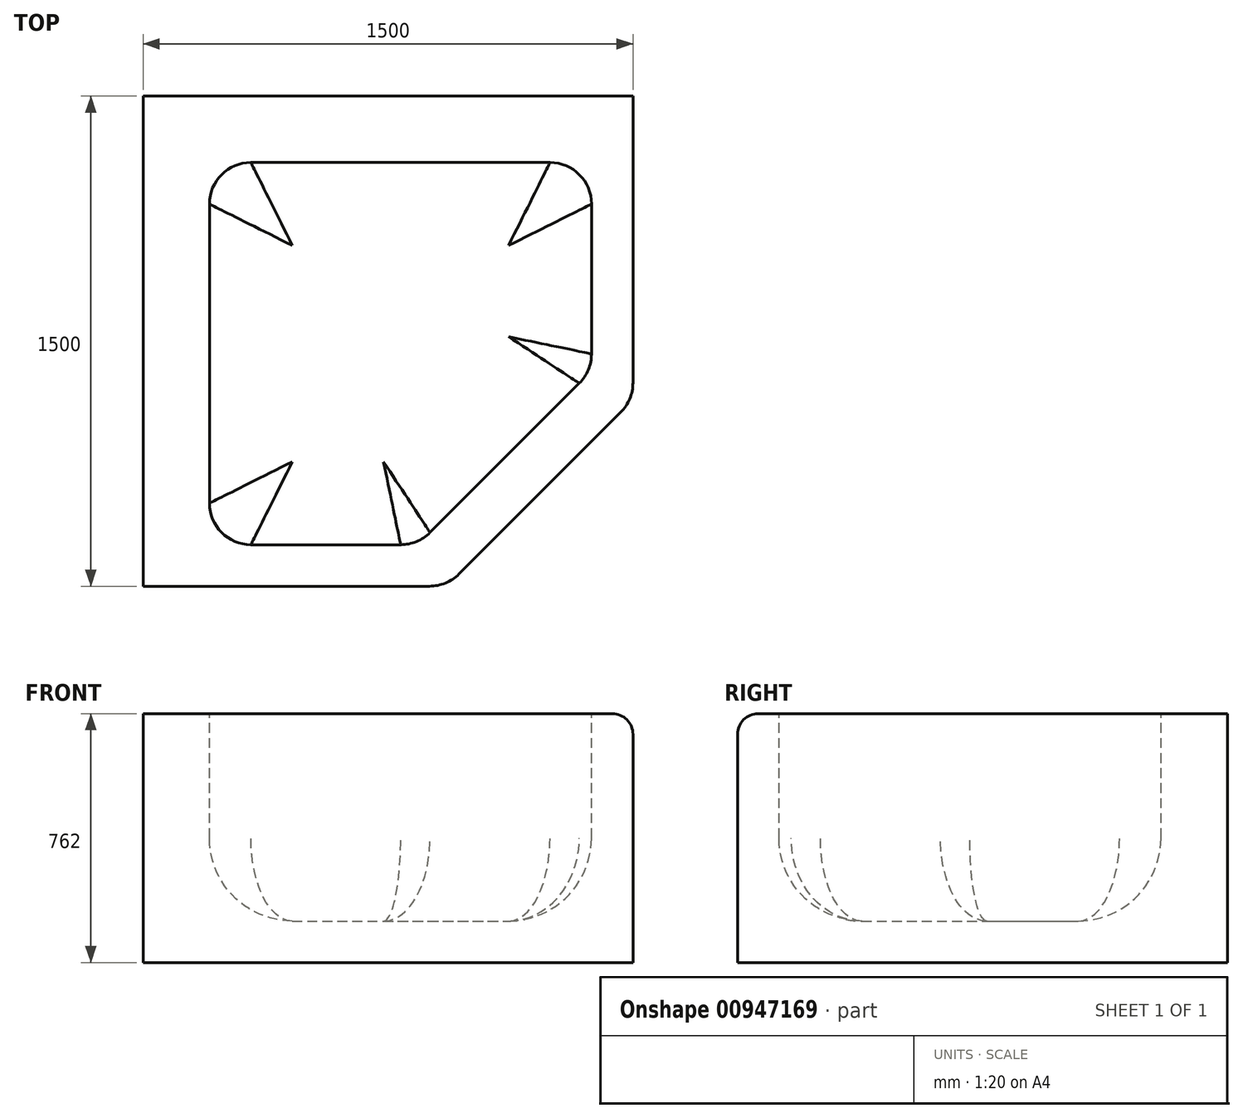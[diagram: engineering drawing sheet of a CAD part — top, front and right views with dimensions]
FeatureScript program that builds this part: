
annotation { "Feature Type Name" : "Feature", "Feature Type Description" : "" }
export const myFeature = defineFeature(function(context is Context, id is Id, definition is map)
    precondition{}
    {
        {
            var Q0;
            Q0=qCreatedBy(makeId("Top.planeOp"),FACE);
            var sketch = newSketch(context, id + "F0", { "sketchPlane" : qUnion([Q0])});
            skLineSegment(sketch, "E0", {"start": v(0, 0) * mm, "end": v(-1500, 0) * mm});
            skLineSegment(sketch, "E1", {"start": v(-1500, 0) * mm, "end": v(-1500, -1500) * mm});
            skLineSegment(sketch, "E2", {"start": v(-1500, -1500) * mm, "end": v(-570, -1500) * mm});
            skLineSegment(sketch, "E3", {"start": v(0, 0) * mm, "end": v(0, -930) * mm});
            skLineSegment(sketch, "E4", {"start": v(-570, -1500) * mm, "end": v(0, -930) * mm});
            skSolve(sketch);
        }
        {
            var Q0;
            Q0 = qSketchRegion(id + "F0", true);
            extrude(context, id + "F1", {"entities" : qUnion([Q0]), "depth" : 762 * mm, "offsetDistance" : 25.4 * mm});
        }
        {
            var Q0;
            Q0=makeQuery(id+"F1.opExtrude","CAP_FACE",FACE,{"disambiguationData":[OSD([sQuery(id+"F0.wireOp",EDGE,"E0"),sQuery(id+"F0.wireOp",EDGE,"E1"),sQuery(id+"F0.wireOp",EDGE,"E2"),sQuery(id+"F0.wireOp",EDGE,"E3"),sQuery(id+"F0.wireOp",EDGE,"E4")])],"isStart":false});
            var sketch = newSketch(context, id + "F2", { "sketchPlane" : qUnion([Q0])});
            skLineSegment(sketch, "E5", {"start": v(-1296.8, -1373) * mm, "end": v(-658.53, -1373) * mm});
            skLineSegment(sketch, "E6", {"start": v(-658.53, -1373) * mm, "end": v(-127, -841.47) * mm});
            skLineSegment(sketch, "E7", {"start": v(-127, -841.47) * mm, "end": v(-127, -203.2) * mm});
            skLineSegment(sketch, "E8", {"start": v(-1296.8, -1373) * mm, "end": v(-1296.8, -203.2) * mm});
            skLineSegment(sketch, "E9", {"start": v(-1296.8, -203.2) * mm, "end": v(-127, -203.2) * mm});
            skSolve(sketch);
        }
        {
            var Q0;
            Q0 = qSketchRegion(id + "F2", true);
            extrude(context, id + "F3", {"entities" : qUnion([Q0]), "operationType" : NewBodyOperationType.REMOVE, "oppositeDirection" : true, "depth" : 635 * mm, "offsetDistance" : 25.4 * mm});
        }
        {
            var Q0;
            Q0=makeQuery(id+"F3.boolean.opBoolean","COPY",EDGE,{"derivedFrom":makeQuery(id+"F3.opExtrude","CAP_EDGE",EDGE,{"disambiguationData":[OSD([sQuery(id+"F2.wireOp",EDGE,"E9")])],"isStart":false})});
            var Q1;
            Q1=makeQuery(id+"F3.boolean.opBoolean","COPY",EDGE,{"derivedFrom":makeQuery(id+"F3.opExtrude","CAP_EDGE",EDGE,{"disambiguationData":[OSD([sQuery(id+"F2.wireOp",EDGE,"E8")])],"isStart":false})});
            var Q2;
            Q2=makeQuery(id+"F3.boolean.opBoolean","COPY",EDGE,{"derivedFrom":makeQuery(id+"F3.opExtrude","CAP_EDGE",EDGE,{"disambiguationData":[OSD([sQuery(id+"F2.wireOp",EDGE,"E5")])],"isStart":false})});
            var Q3;
            Q3=makeQuery(id+"F3.boolean.opBoolean","COPY",EDGE,{"derivedFrom":makeQuery(id+"F3.opExtrude","CAP_EDGE",EDGE,{"disambiguationData":[OSD([sQuery(id+"F2.wireOp",EDGE,"E6")])],"isStart":false})});
            var Q4;
            Q4=makeQuery(id+"F3.boolean.opBoolean","COPY",EDGE,{"derivedFrom":makeQuery(id+"F3.opExtrude","CAP_EDGE",EDGE,{"disambiguationData":[OSD([sQuery(id+"F2.wireOp",EDGE,"E7")])],"isStart":false})});
            fillet(context, id + "F4", {"entities" : qUnion([Q0, Q1, Q2, Q3, Q4]), "radius" : 254 * mm, "tangentPropagation" : true, "allowEdgeOverflow" : false});
        }
        {
            var Q0;
            Q0=makeQuery(id+"F1.opExtrude","CAP_EDGE",EDGE,{"disambiguationData":[OSD([sQuery(id+"F0.wireOp",EDGE,"E2")])],"isStart":false});
            var Q1;
            Q1=makeQuery(id+"F1.opExtrude","CAP_EDGE",EDGE,{"disambiguationData":[OSD([sQuery(id+"F0.wireOp",EDGE,"E4")])],"isStart":false});
            var Q2;
            Q2=makeQuery(id+"F1.opExtrude","CAP_EDGE",EDGE,{"disambiguationData":[OSD([sQuery(id+"F0.wireOp",EDGE,"E3")])],"isStart":false});
            var Q3;
            Q3=makeQuery(id+"F3.boolean.opBoolean","COPY",EDGE,{"derivedFrom":makeQuery(id+"F3.opExtrude","CAP_EDGE",EDGE,{"disambiguationData":[OSD([sQuery(id+"F2.wireOp",EDGE,"E5")])],"isStart":true})});
            var Q4;
            Q4=makeQuery(id+"F3.boolean.opBoolean","COPY",EDGE,{"derivedFrom":makeQuery(id+"F3.opExtrude","CAP_EDGE",EDGE,{"disambiguationData":[OSD([sQuery(id+"F2.wireOp",EDGE,"E8")])],"isStart":true})});
            var Q5;
            Q5=makeQuery(id+"F3.boolean.opBoolean","COPY",EDGE,{"derivedFrom":makeQuery(id+"F3.opExtrude","CAP_EDGE",EDGE,{"disambiguationData":[OSD([sQuery(id+"F2.wireOp",EDGE,"E9")])],"isStart":true})});
            var Q6;
            Q6=makeQuery(id+"F3.boolean.opBoolean","COPY",EDGE,{"derivedFrom":makeQuery(id+"F3.opExtrude","CAP_EDGE",EDGE,{"disambiguationData":[OSD([sQuery(id+"F2.wireOp",EDGE,"E7")])],"isStart":true})});
            var Q7;
            Q7=makeQuery(id+"F3.boolean.opBoolean","COPY",EDGE,{"derivedFrom":makeQuery(id+"F3.opExtrude","CAP_EDGE",EDGE,{"disambiguationData":[OSD([sQuery(id+"F2.wireOp",EDGE,"E6")])],"isStart":true})});
            fillet(context, id + "F5", {"entities" : qUnion([Q0, Q1, Q2, Q3, Q4, Q5, Q6, Q7]), "radius" : 63.5 * mm, "tangentPropagation" : true, "allowEdgeOverflow" : false});
        }
        {
            var Q0;
            Q0=makeQuery(id+"F3.boolean.opBoolean","COPY",EDGE,{"derivedFrom":makeQuery(id+"F3.opExtrude","SWEPT_EDGE",EDGE,{"disambiguationData":[OSD([sQuery(id+"F2.wireOp",EDGE,"E6"),sQuery(id+"F2.wireOp",EDGE,"E7")])]})});
            var Q1;
            Q1=makeQuery(id+"F3.boolean.opBoolean","COPY",EDGE,{"derivedFrom":makeQuery(id+"F3.opExtrude","SWEPT_EDGE",EDGE,{"disambiguationData":[OSD([sQuery(id+"F2.wireOp",EDGE,"E7"),sQuery(id+"F2.wireOp",EDGE,"E9")])]})});
            var Q2;
            Q2=makeQuery(id+"F3.boolean.opBoolean","COPY",EDGE,{"derivedFrom":makeQuery(id+"F3.opExtrude","SWEPT_EDGE",EDGE,{"disambiguationData":[OSD([sQuery(id+"F2.wireOp",EDGE,"E5"),sQuery(id+"F2.wireOp",EDGE,"E6")])]})});
            var Q3;
            Q3=makeQuery(id+"F3.boolean.opBoolean","COPY",EDGE,{"derivedFrom":makeQuery(id+"F3.opExtrude","SWEPT_EDGE",EDGE,{"disambiguationData":[OSD([sQuery(id+"F2.wireOp",EDGE,"E5"),sQuery(id+"F2.wireOp",EDGE,"E8")])]})});
            var Q4;
            Q4=makeQuery(id+"F3.boolean.opBoolean","COPY",EDGE,{"derivedFrom":makeQuery(id+"F3.opExtrude","SWEPT_EDGE",EDGE,{"disambiguationData":[OSD([sQuery(id+"F2.wireOp",EDGE,"E8"),sQuery(id+"F2.wireOp",EDGE,"E9")])]})});
            fillet(context, id + "F6", {"entities" : qUnion([Q0, Q1, Q2, Q3, Q4]), "radius" : 127 * mm, "tangentPropagation" : true, "allowEdgeOverflow" : false});
        }
        {
            var Q0;
            Q0=makeQuery(id+"F1.opExtrude","SWEPT_EDGE",EDGE,{"disambiguationData":[OSD([sQuery(id+"F0.wireOp",EDGE,"E2"),sQuery(id+"F0.wireOp",EDGE,"E4")])]});
            var Q1;
            Q1=makeQuery(id+"F1.opExtrude","SWEPT_EDGE",EDGE,{"disambiguationData":[OSD([sQuery(id+"F0.wireOp",EDGE,"E3"),sQuery(id+"F0.wireOp",EDGE,"E4")])]});
            fillet(context, id + "F7", {"entities" : qUnion([Q0, Q1]), "radius" : 127 * mm, "tangentPropagation" : true, "allowEdgeOverflow" : false});
        }
    });
